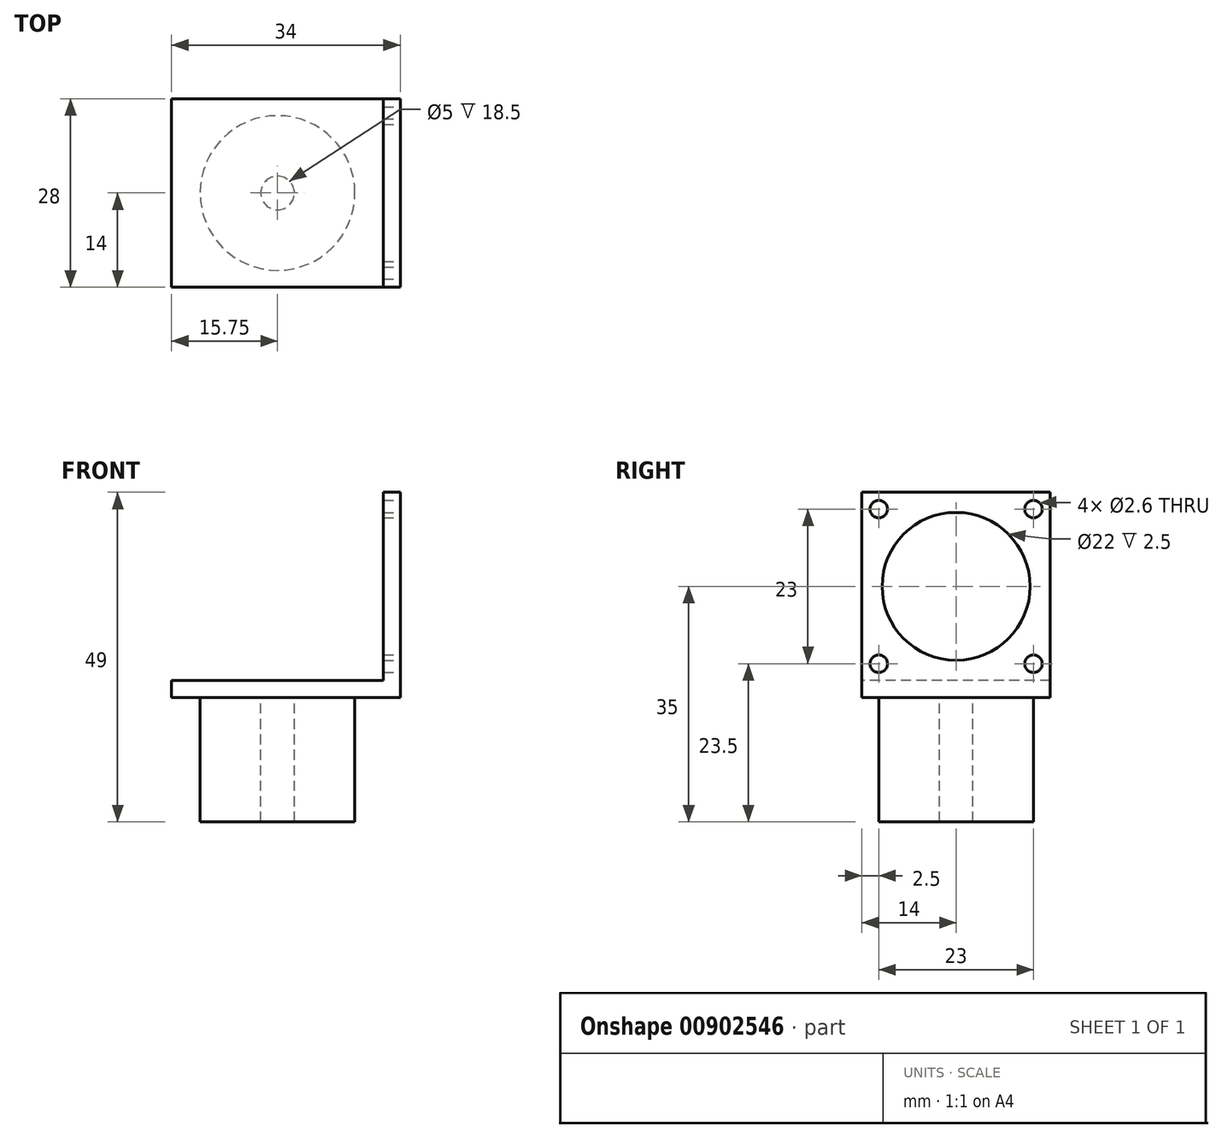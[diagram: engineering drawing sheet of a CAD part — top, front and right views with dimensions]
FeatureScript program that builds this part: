
annotation { "Feature Type Name" : "Feature", "Feature Type Description" : "" }
export const myFeature = defineFeature(function(context is Context, id is Id, definition is map)
    precondition{}
    {
        {
            var Q0;
            Q0=qCreatedBy(makeId("Top.planeOp"),FACE);
            var sketch = newSketch(context, id + "F0", { "sketchPlane" : qUnion([Q0])});
            skLineSegment(sketch, "E0.bottom", {"start": v(15.75, 14) * mm, "end": v(-15.75, 14) * mm});
            skLineSegment(sketch, "E0.top", {"start": v(15.75, -14) * mm, "end": v(-15.75, -14) * mm});
            skLineSegment(sketch, "E0.left", {"start": v(15.75, 14) * mm, "end": v(15.75, -14) * mm});
            skLineSegment(sketch, "E0.right", {"start": v(-15.75, 14) * mm, "end": v(-15.75, -14) * mm});
            skPoint(sketch, "E0.middle", {"position": v(0, 0) * mm});
            skLineSegment(sketch, "E1.bottom", {"start": v(15.75, 14) * mm, "end": v(18.25, 14) * mm});
            skLineSegment(sketch, "E1.top", {"start": v(15.75, -14) * mm, "end": v(18.25, -14) * mm});
            skLineSegment(sketch, "E1.right", {"start": v(18.25, 14) * mm, "end": v(18.25, -14) * mm});
            skSolve(sketch);
        }
        {
            var Q0;
            Q0=makeQuery(id+"F0.imprint","IMPRINT",FACE,{"disambiguationData":[TD([[makeQuery(id+"F0.imprint","IMPRINT",EDGE,{"derivedFrom":sQuery(id+"F0.wireOp",EDGE,"E0.bottom")}),1.0]])]});
            extrude(context, id + "F1", {"entities" : qUnion([Q0]), "depth" : 2.5 * mm, "offsetDistance" : 25 * mm});
        }
        {
            var Q0;
            Q0=makeQuery(id+"F0.imprint","IMPRINT",FACE,{"disambiguationData":[TD([[makeQuery(id+"F0.imprint","IMPRINT",EDGE,{"derivedFrom":sQuery(id+"F0.wireOp",EDGE,"E1.bottom")}),-1.0]])]});
            extrude(context, id + "F2", {"entities" : qUnion([Q0]), "operationType" : NewBodyOperationType.ADD, "depth" : 30.5 * mm, "offsetDistance" : 25 * mm});
        }
        {
            var Q0;
            Q0=makeQuery(id+"F2.opExtrude","SWEPT_FACE",FACE,{"disambiguationData":[OSD([sQuery(id+"F0.wireOp",EDGE,"E1.right")])]});
            var sketch = newSketch(context, id + "F3", { "sketchPlane" : qUnion([Q0])});
            skLineSegment(sketch, "E2", {"start": v(0, 30.5) * mm, "end": v(0, 16.5) * mm});
            skCircle(sketch, "E3", {"center": v(0, 16.5) * mm, "radius": 11 * mm});
            skLineSegment(sketch, "E4.bottom", {"start": v(11.5, 28) * mm, "end": v(-11.5, 28) * mm});
            skLineSegment(sketch, "E4.top", {"start": v(11.5, 5) * mm, "end": v(-11.5, 5) * mm});
            skLineSegment(sketch, "E4.left", {"start": v(11.5, 28) * mm, "end": v(11.5, 5) * mm});
            skLineSegment(sketch, "E4.right", {"start": v(-11.5, 28) * mm, "end": v(-11.5, 5) * mm});
            skCircle(sketch, "E5", {"center": v(-11.5, 28) * mm, "radius": 1.3 * mm});
            skCircle(sketch, "E6", {"center": v(11.5, 28) * mm, "radius": 1.3 * mm});
            skCircle(sketch, "E7", {"center": v(11.5, 5) * mm, "radius": 1.3 * mm});
            skCircle(sketch, "E8", {"center": v(-11.5, 5) * mm, "radius": 1.3 * mm});
            skSolve(sketch);
        }
        {
            var Q0;
            {var subQ0=sQuery(id+"F3.wireOp",EDGE,"E4.right");var subQ1=sQuery(id+"F3.wireOp",EDGE,"E4.bottom");var subQ2=makeQuery(id+"F3.imprint","INTERSECT",VERTEX,{"derivedFrom":[subQ1,subQ0]});Q0=makeQuery(id+"F3.imprint","IMPRINT",FACE,{"disambiguationData":[TD([[makeQuery(id+"F3.imprint","IMPRINT",EDGE,{"disambiguationData":[TD([[subQ2,1.0]])],"derivedFrom":subQ1}),-1.0]])]});}
            var Q1;
            {var subQ0=sQuery(id+"F3.wireOp",EDGE,"E4.right");var subQ1=sQuery(id+"F3.wireOp",EDGE,"E4.top");var subQ2=makeQuery(id+"F3.imprint","INTERSECT",VERTEX,{"derivedFrom":[subQ1,subQ0]});Q1=makeQuery(id+"F3.imprint","IMPRINT",FACE,{"disambiguationData":[TD([[makeQuery(id+"F3.imprint","IMPRINT",EDGE,{"disambiguationData":[TD([[subQ2,1.0]])],"derivedFrom":subQ1}),1.0]])]});}
            var Q2;
            {var subQ0=sQuery(id+"F3.wireOp",EDGE,"E4.right");var subQ1=sQuery(id+"F3.wireOp",EDGE,"E4.top");var subQ2=makeQuery(id+"F3.imprint","INTERSECT",VERTEX,{"derivedFrom":[subQ1,subQ0]});Q2=makeQuery(id+"F3.imprint","IMPRINT",FACE,{"disambiguationData":[TD([[makeQuery(id+"F3.imprint","IMPRINT",EDGE,{"disambiguationData":[TD([[subQ2,1.0]])],"derivedFrom":subQ1}),-1.0]])]});}
            var Q3;
            {var subQ0=sQuery(id+"F3.wireOp",EDGE,"E4.left");var subQ1=sQuery(id+"F3.wireOp",EDGE,"E4.top");var subQ2=makeQuery(id+"F3.imprint","INTERSECT",VERTEX,{"derivedFrom":[subQ1,subQ0]});Q3=makeQuery(id+"F3.imprint","IMPRINT",FACE,{"disambiguationData":[TD([[makeQuery(id+"F3.imprint","IMPRINT",EDGE,{"disambiguationData":[TD([[subQ2,-1.0]])],"derivedFrom":subQ1}),-1.0]])]});}
            var Q4;
            {var subQ0=sQuery(id+"F3.wireOp",EDGE,"E4.left");var subQ1=sQuery(id+"F3.wireOp",EDGE,"E4.top");var subQ2=makeQuery(id+"F3.imprint","INTERSECT",VERTEX,{"derivedFrom":[subQ1,subQ0]});Q4=makeQuery(id+"F3.imprint","IMPRINT",FACE,{"disambiguationData":[TD([[makeQuery(id+"F3.imprint","IMPRINT",EDGE,{"disambiguationData":[TD([[subQ2,-1.0]])],"derivedFrom":subQ1}),1.0]])]});}
            var Q5;
            Q5=makeQuery(id+"F3.imprint","IMPRINT",FACE,{"disambiguationData":[TD([[makeQuery(id+"F3.imprint","IMPRINT",EDGE,{"derivedFrom":sQuery(id+"F3.wireOp",EDGE,"E3")}),1.0]])]});
            var Q6;
            {var subQ0=sQuery(id+"F3.wireOp",EDGE,"E4.right");var subQ1=sQuery(id+"F3.wireOp",EDGE,"E4.bottom");var subQ2=makeQuery(id+"F3.imprint","INTERSECT",VERTEX,{"derivedFrom":[subQ1,subQ0]});Q6=makeQuery(id+"F3.imprint","IMPRINT",FACE,{"disambiguationData":[TD([[makeQuery(id+"F3.imprint","IMPRINT",EDGE,{"disambiguationData":[TD([[subQ2,1.0]])],"derivedFrom":subQ1}),1.0]])]});}
            var Q7;
            {var subQ0=sQuery(id+"F3.wireOp",EDGE,"E4.left");var subQ1=sQuery(id+"F3.wireOp",EDGE,"E4.bottom");var subQ2=makeQuery(id+"F3.imprint","INTERSECT",VERTEX,{"derivedFrom":[subQ1,subQ0]});Q7=makeQuery(id+"F3.imprint","IMPRINT",FACE,{"disambiguationData":[TD([[makeQuery(id+"F3.imprint","IMPRINT",EDGE,{"disambiguationData":[TD([[subQ2,-1.0]])],"derivedFrom":subQ1}),1.0]])]});}
            var Q8;
            {var subQ0=sQuery(id+"F3.wireOp",EDGE,"E4.left");var subQ1=sQuery(id+"F3.wireOp",EDGE,"E4.bottom");var subQ2=makeQuery(id+"F3.imprint","INTERSECT",VERTEX,{"derivedFrom":[subQ1,subQ0]});Q8=makeQuery(id+"F3.imprint","IMPRINT",FACE,{"disambiguationData":[TD([[makeQuery(id+"F3.imprint","IMPRINT",EDGE,{"disambiguationData":[TD([[subQ2,-1.0]])],"derivedFrom":subQ1}),-1.0]])]});}
            extrude(context, id + "F4", {"entities" : qUnion([Q0, Q1, Q2, Q3, Q4, Q5, Q6, Q7, Q8]), "operationType" : NewBodyOperationType.REMOVE, "oppositeDirection" : true, "depth" : 2.5 * mm, "offsetDistance" : 25 * mm});
        }
        {
            var Q0;
            {var subQ0=sQuery(id+"F0.wireOp",EDGE,"E0.left");Q0=makeQuery(id+"F2.boolean.opBoolean","MERGE",FACE,{"derivedFrom":[makeQuery(id+"F1.opExtrude","CAP_FACE",FACE,{"disambiguationData":[OSD([sQuery(id+"F0.wireOp",EDGE,"E0.bottom"),sQuery(id+"F0.wireOp",EDGE,"E0.top"),sQuery(id+"F0.wireOp",EDGE,"E0.right"),subQ0])],"isStart":true}),makeQuery(id+"F2.opExtrude","CAP_FACE",FACE,{"disambiguationData":[OSD([sQuery(id+"F0.wireOp",EDGE,"E1.bottom"),sQuery(id+"F0.wireOp",EDGE,"E1.top"),subQ0,sQuery(id+"F0.wireOp",EDGE,"E1.right")])],"isStart":true})]});}
            var sketch = newSketch(context, id + "F5", { "sketchPlane" : qUnion([Q0])});
            skCircle(sketch, "E9", {"center": v(0, 0) * mm, "radius": 11.5 * mm});
            skCircle(sketch, "E10", {"center": v(0, 0) * mm, "radius": 2.5 * mm});
            skSolve(sketch);
        }
        {
            var Q0;
            Q0=makeQuery(id+"F5.imprint","IMPRINT",FACE,{"disambiguationData":[TD([[makeQuery(id+"F5.imprint","IMPRINT",EDGE,{"derivedFrom":sQuery(id+"F5.wireOp",EDGE,"E9")}),1.0]])]});
            extrude(context, id + "F6", {"entities" : qUnion([Q0]), "operationType" : NewBodyOperationType.ADD, "depth" : 18.5 * mm, "offsetDistance" : 25 * mm});
        }
    });
